# Revit family: Linkeo Freestanding cabinets with double front door width 800
name_source: partatom
category: Equipement spécialisé
units: mm (PartAtom-declared; Revit-internal decimal feet)

## family parameters
Basée sur le plan de construction = Non
Cote de connecteur circulaire = Utiliser le diamètre
Couper avec des vides une fois chargée = Non
Numéro OmniClass = 23.85.05.17.11.14
Partagée = Oui
Point de calcul de pièce = Non
Titre OmniClass = Multimedia Broadcasting Equipment
Toujours verticalement = Oui
Type d'élément = Normal

## types (3) — shared parameters
Application class = EC002499
Avec porte frontale = Oui
Color = grey
Degree of protection IK = IK08
Degree of protection IP = IP20
Door symbol = Door symbol  Double front door
E-catalogue link = https://www.legrand.fr
Fabricant = Legrand
Front door material = glass
Function = Cabinet Linkeo2
Height = 2026 mm  [stored 6.64698 ft]
Locking of the front door = One point
Material = Steel
Max load capacity = 400
Model = With permanent frame
Model width = 800 mm  [stored 2.62467 ft]
Modular spacing = 19 inches
Mounting level = Front side
Number of doors = 2
Number of height units = 42
Operating temperature = -25°C à 70°C
RAL Number = 7016
Rack location = 93 mm  [stored 0.305118 ft]
Storage temperature = -25°C à 70°C
Type of profile rail = Crank
Type of surface = Powder coating
Type of ventilation = None
Type of vertical uprights = Vertical uprights for Linkeo freestanding cabinets  42U
Width (mm) = 810 mm
With earthing = Oui
With roof plate = Oui
zero-valued in all types: Elévation par défaut

## per-type parameters (varying)
| type | Depth | Depth of the model (mm) | Distance of the aperture 1 | Distance of the aperture 2 | EAN | Legrand part number | Type of horizontal uprights | Type of levelling feet | Usable height (mm) | Usable width (mm) |
| Cabinet Linkeo2 42U 800x600 double door | 630 mm  [stored 2.06693 ft] | 600 mm | 57 mm  [stored 0.187008 ft] | 98 mm  [stored 0.321522 ft] | 3414971001602 | 646766 | Horizontal uprights for Linkeo freestanding cabinets  42U depth 600 | Levelling feet  800X600 | 1786 mm  [stored 5.85958 ft] | 490 mm  [stored 1.60761 ft] |
| Cabinet Linkeo2 42U 800x800 double door | 830 mm  [stored 2.7231 ft] | 800 mm  [stored 2.62467 ft] | 257 mm  [stored 0.843176 ft] | 198 mm  [stored 0.649606 ft] | 3414971001619 | 646767 | Horizontal uprights for Linkeo freestanding cabinets  42U depth 800 | Levelling feet  800X800 | 1786 mm  [stored 5.85958 ft] | 690 mm  [stored 2.26378 ft] |
| Cabinet Linkeo2 42U 800x1000 double door | 1030 mm  [stored 3.37927 ft] | 1000 mm  [stored 3.28084 ft] | 457 mm  [stored 1.49934 ft] | 298 mm  [stored 0.97769 ft] | 3414971001626 | 646768 | Horizontal uprights for Linkeo freestanding cabinets  42U depth 1000 | Levelling feet  800X1000 | 1881 mm  [stored 6.17126 ft] | 890 mm  [stored 2.91995 ft] |

note: column(s) folded — value = type name in every type: BIM wording

note: [stored X ft] marks values corroborated as IEEE doubles in the binary element streams (Revit-internal decimal feet)
